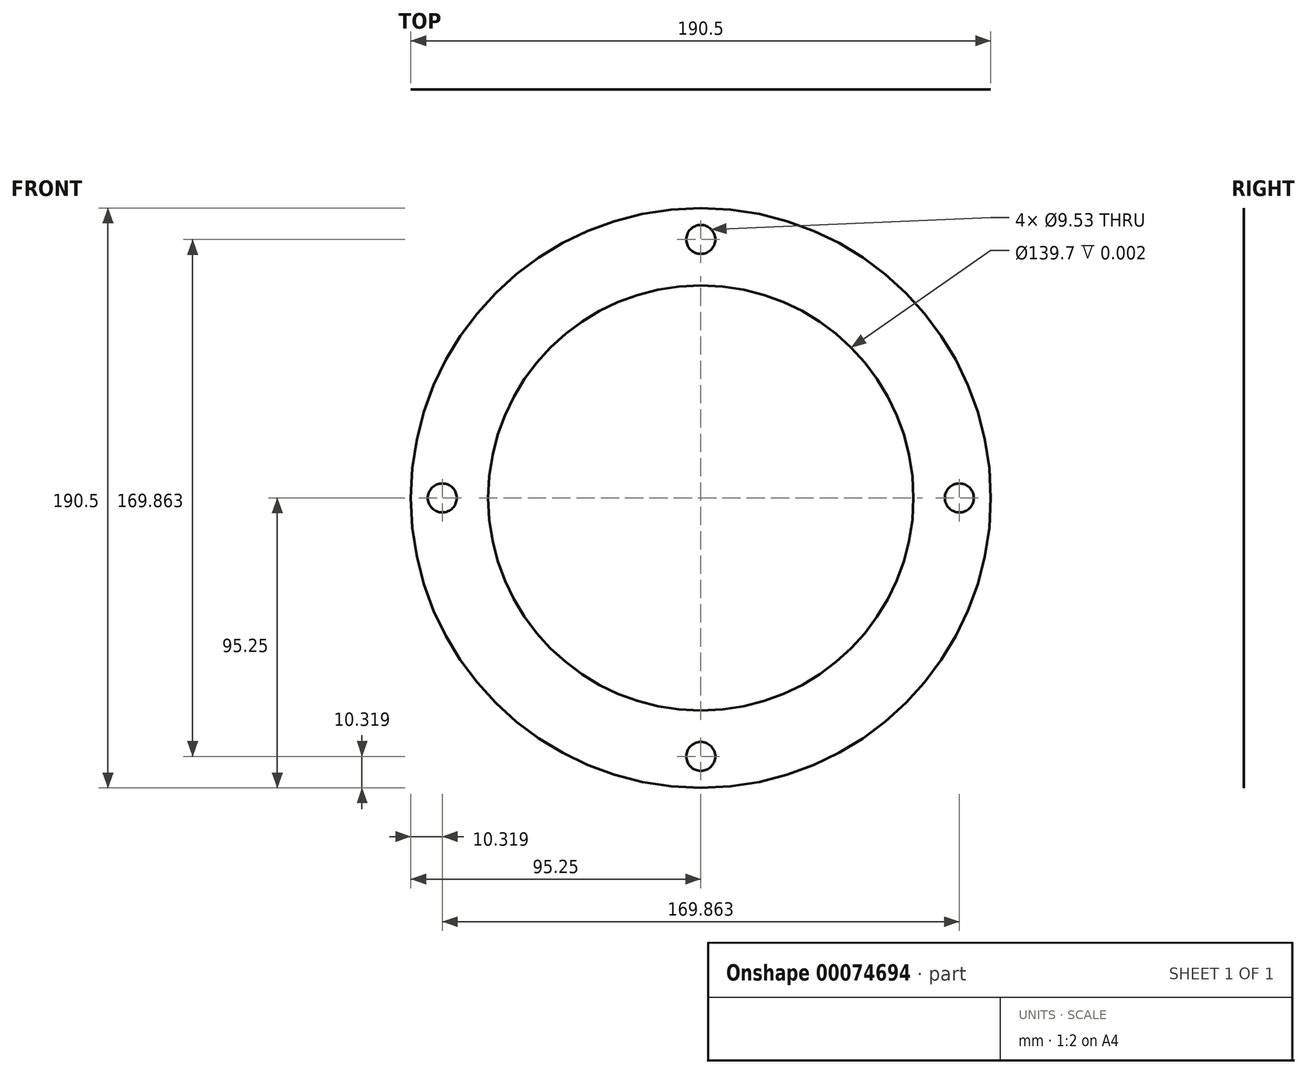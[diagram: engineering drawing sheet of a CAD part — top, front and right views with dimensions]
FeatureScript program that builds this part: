
annotation { "Feature Type Name" : "Feature", "Feature Type Description" : "" }
export const myFeature = defineFeature(function(context is Context, id is Id, definition is map)
    precondition{}
    {
        {
            var Q0;
            Q0=qCreatedBy(makeId("Front.planeOp"),FACE);
            var sketch = newSketch(context, id + "F0", { "sketchPlane" : qUnion([Q0])});
            skCircle(sketch, "E0", {"center": v(0, 0) * mm, "radius": 95.25 * mm});
            skCircle(sketch, "E1", {"center": v(0, 0) * mm, "radius": 69.85 * mm});
            skCircle(sketch, "E2", {"center": v(0, 84.93) * mm, "radius": 4.76 * mm});
            skCircle(sketch, "E3.1.0", {"center": v(-84.93, 0) * mm, "radius": 4.76 * mm});
            skCircle(sketch, "E3.2.0", {"center": v(0, -84.93) * mm, "radius": 4.76 * mm});
            skCircle(sketch, "E3.3.0", {"center": v(84.93, 0) * mm, "radius": 4.76 * mm});
            skSolve(sketch);
        }
        {
            var Q0;
            Q0=makeQuery(id+"F0.imprint","IMPRINT",FACE,{"disambiguationData":[TD([[makeQuery(id+"F0.imprint","IMPRINT",EDGE,{"derivedFrom":sQuery(id+"F0.wireOp",EDGE,"E0")}),1.0]])]});
            extrude(context, id + "F1", {"entities" : qUnion([Q0]), "depth" : 1 / 406.4 * mm});
        }
    });
